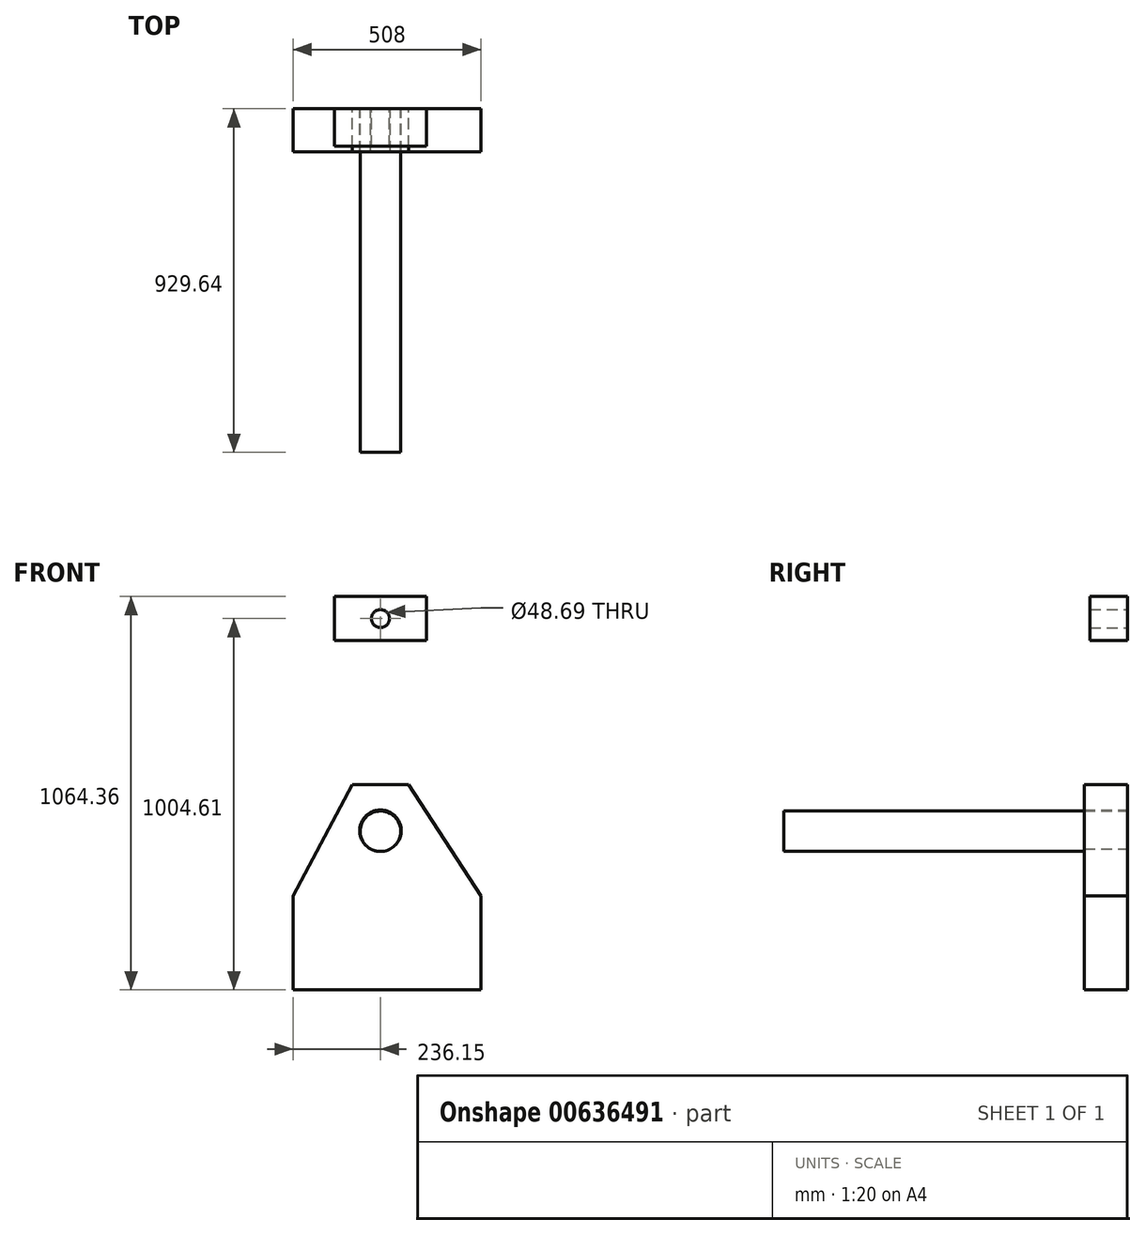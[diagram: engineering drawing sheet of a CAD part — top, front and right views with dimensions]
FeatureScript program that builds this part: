
annotation { "Feature Type Name" : "Feature", "Feature Type Description" : "" }
export const myFeature = defineFeature(function(context is Context, id is Id, definition is map)
    precondition{}
    {
        {
            var Q0;
            Q0=qCreatedBy(makeId("Front.planeOp"),FACE);
            var sketch = newSketch(context, id + "F0", { "sketchPlane" : qUnion([Q0])});
            skLineSegment(sketch, "E0", {"start": v(-236.15, 0) * mm, "end": v(271.85, 0) * mm});
            skLineSegment(sketch, "E1", {"start": v(-236.15, 0) * mm, "end": v(-236.15, 254) * mm});
            skLineSegment(sketch, "E2", {"start": v(-76.2, 556.1) * mm, "end": v(0, 556.1) * mm});
            skLineSegment(sketch, "E3", {"start": v(0, 556.1) * mm, "end": v(76.2, 556.1) * mm});
            skLineSegment(sketch, "E4", {"start": v(-76.2, 556.1) * mm, "end": v(-236.15, 254) * mm});
            skLineSegment(sketch, "E5", {"start": v(271.85, 0) * mm, "end": v(271.85, 254) * mm});
            skLineSegment(sketch, "E6", {"start": v(76.2, 556.1) * mm, "end": v(271.85, 254) * mm});
            skCircle(sketch, "E7", {"center": v(0, 430.87) * mm, "radius": 56.1 * mm});
            skSolve(sketch);
        }
        {
            var Q0;
            Q0=makeQuery(id+"F0.imprint","IMPRINT",FACE,{"disambiguationData":[TD([[makeQuery(id+"F0.imprint","IMPRINT",EDGE,{"derivedFrom":sQuery(id+"F0.wireOp",EDGE,"E0")}),1.0]])]});
            extrude(context, id + "F1", {"entities" : qUnion([Q0]), "depth" : 116.84 * mm, "offsetDistance" : 25.4 * mm});
        }
        {
            var Q0;
            Q0=qCreatedBy(makeId("Front.planeOp"),FACE);
            var sketch = newSketch(context, id + "F2", { "sketchPlane" : qUnion([Q0])});
            skCircle(sketch, "E8", {"center": v(0, 429.22) * mm, "radius": 54.66 * mm});
            skSolve(sketch);
        }
        {
            var Q0;
            Q0=makeQuery(id+"F2.imprint","IMPRINT",FACE,{"disambiguationData":[TD([[makeQuery(id+"F2.imprint","IMPRINT",EDGE,{"derivedFrom":sQuery(id+"F2.wireOp",EDGE,"E8")}),1.0]])]});
            extrude(context, id + "F3", {"entities" : qUnion([Q0]), "operationType" : NewBodyOperationType.ADD, "depth" : 929.64 * mm, "offsetDistance" : 25.4 * mm});
        }
        {
            var Q0;
            Q0=qCreatedBy(makeId("Front.planeOp"),FACE);
            var sketch = newSketch(context, id + "F4", { "sketchPlane" : qUnion([Q0])});
            skLineSegment(sketch, "E9.bottom", {"start": v(125, 1064.36) * mm, "end": v(-125, 1064.36) * mm});
            skLineSegment(sketch, "E9.top", {"start": v(125, 944.85) * mm, "end": v(-125, 944.85) * mm});
            skLineSegment(sketch, "E9.left", {"start": v(125, 1064.36) * mm, "end": v(125, 944.85) * mm});
            skLineSegment(sketch, "E9.right", {"start": v(-125, 1064.36) * mm, "end": v(-125, 944.85) * mm});
            skPoint(sketch, "E9.middle", {"position": v(0, 1004.6) * mm});
            skCircle(sketch, "E10", {"center": v(0, 1004.6) * mm, "radius": 24.34 * mm});
            skSolve(sketch);
        }
        {
            var Q0;
            Q0 = qSketchRegion(id + "F4", true);
            extrude(context, id + "F5", {"entities" : qUnion([Q0]), "depth" : 101.6 * mm, "offsetDistance" : 25.4 * mm});
        }
    });
